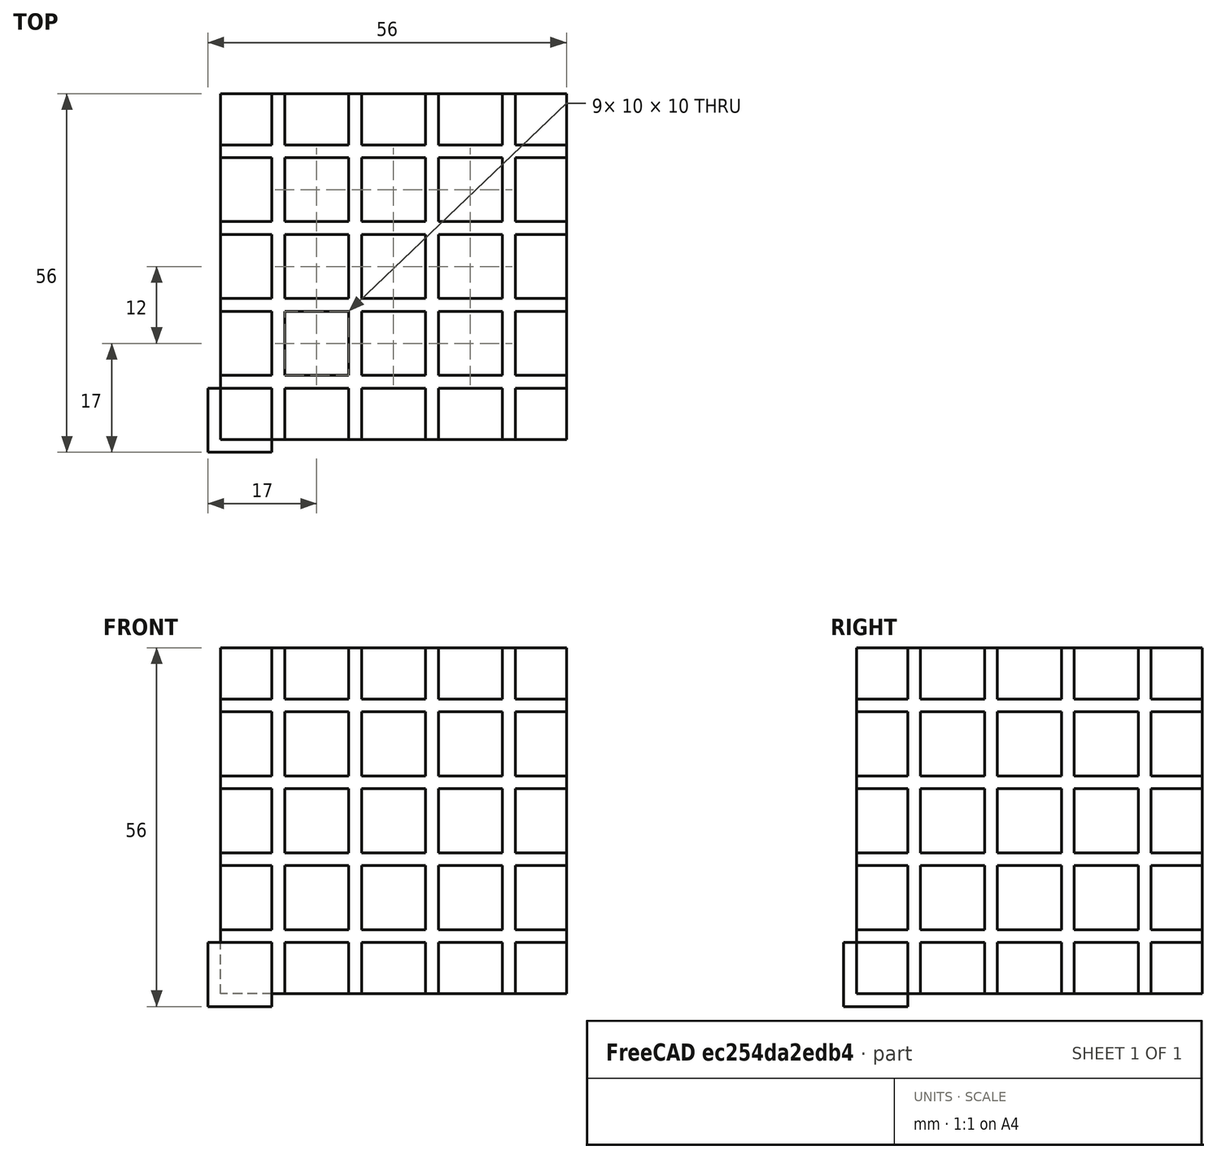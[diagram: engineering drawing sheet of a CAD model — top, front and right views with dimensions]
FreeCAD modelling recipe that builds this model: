
FCSTD DOCUMENT  (FreeCAD 0.21R33694 (Git))
Label: OJT1_T010P09_Z
License: All rights reserved
LicenseURL: http://en.wikipedia.org/wiki/All_rights_reserved
objects: Part::Box×2, Part::FeaturePython×1, Part::Cut×1
note: 3 computed .brp shape members not serialized (recipe doc carries the construction recipe); baked Part::Feature solids carry a one-line shape summary decoded from their .brp

FEATURE [Part::Box] Box  label="Cube"
  AttacherType = Attacher::AttachEngine3D
  Height = 10
  Length = 10
  Width = 10
FEATURE [Part::FeaturePython] Array  # Draft array (typed FeaturePython)
  AlwaysSyncPlacement = false
  Angle = 360
  ArrayType = 0
  Axis = (0,0,1)
  Base = -> Box
  Center = (0,0,0)
  Count = 125
  ExpandArray = false
  Fuse = false
  IntervalAxis = (0,0,0)
  IntervalX = (12,0,0)
  IntervalY = (0,12,0)
  IntervalZ = (0,0,12)
  NumberCircles = 3
  NumberPolar = 5
  NumberX = 5
  NumberY = 5
  NumberZ = 5
  PlacementList = 125 placements: [(0,0,0),(0,0,12),(0,0,24),(0,0,36),(0,0,48),(0,12,0),(0,12,12),(0,12,24),(0,12,36),(0,12,48),(0,24,0),(0,24,12),(0,24,24),(0,24,36),(0,24,48),(0,36,0),(0,36,12),(0,36,24),(0,36,36),(0,36,48),(0,48,0),(0,48,12),(0,48,24),(0,48,36),(0,48,48),(12,0,0),(12,0,12),(12,0,24),(12,0,36),(12,0,48),(12,12,0),(12,12,12),(12,12,24),(12,12,36),(12,12,48),(12,24,0),(12,24,12),(12,24,24),(12,24,36),(12,24,48),+85 more]
  RadialDistance = 50
  ScaleList = (125) [(1,1,1),(1,1,1),(1,1,1),(1,1,1),(1,1,1),(1,1,1),(1,1,1),(1,1,1),(1,1,1),(1,1,1),(1,1,1),(1,1,1),(1,1,1),(1,1,1),(1,1,1),(1,1,1),(1,1,1),(1,1,1),+107 more]
  Symmetry = 1
  TangentialDistance = 25
FEATURE [Part::Box] Box001  label="Cube001"
  AttacherType = Attacher::AttachEngine3D
  Height = 54
  Length = 54
  Placement = pos=(2,2,2) rot=(0,0,1;0rad)
  Width = 54
FEATURE [Part::Cut] Cut
  Base = -> Box001
  Refine = true
  Tool = -> Array
